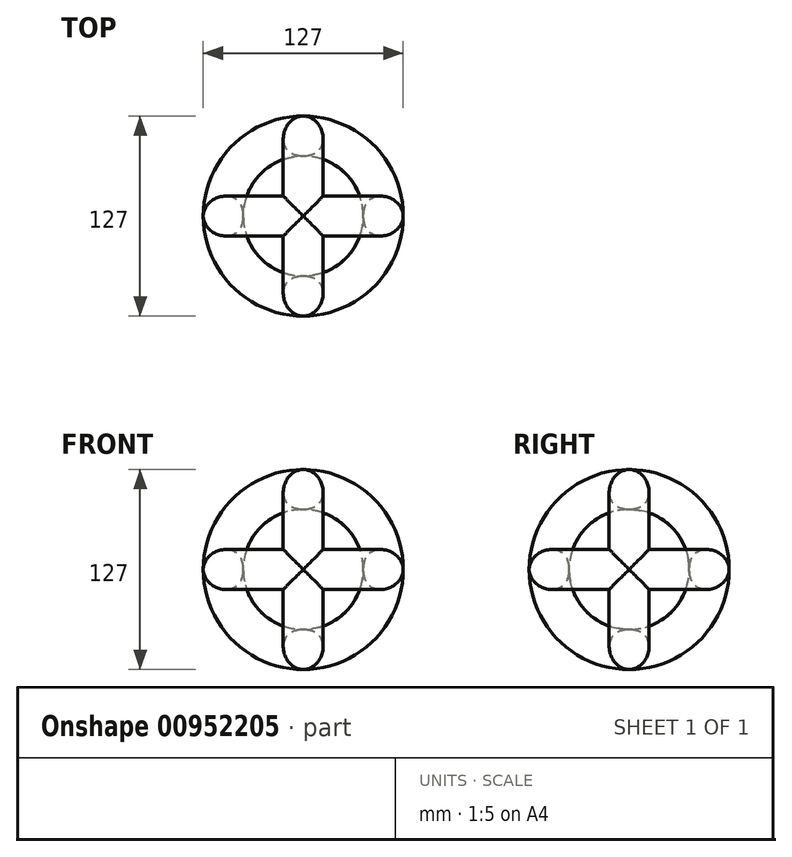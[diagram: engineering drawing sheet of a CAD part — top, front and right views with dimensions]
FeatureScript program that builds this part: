
annotation { "Feature Type Name" : "Feature", "Feature Type Description" : "" }
export const myFeature = defineFeature(function(context is Context, id is Id, definition is map)
    precondition{}
    {
        {
            var Q0;
            Q0=qCreatedBy(makeId("Front.planeOp"),FACE);
            var sketch = newSketch(context, id + "F0", { "sketchPlane" : qUnion([Q0])});
            skCircle(sketch, "E0", {"center": v(50.8, 0) * mm, "radius": 12.7 * mm});
            skCircle(sketch, "E1.1.0", {"center": v(0, 50.8) * mm, "radius": 12.7 * mm});
            skPoint(sketch, "E1.center", {"position": v(0, 0) * mm});
            skSolve(sketch);
        }
        {
            var Q0;
            Q0=qCreatedBy(makeId("Right.planeOp"),FACE);
            var sketch = newSketch(context, id + "F1", { "sketchPlane" : qUnion([Q0])});
            skCircle(sketch, "E2", {"center": v(0, 0) * mm, "radius": 50.8 * mm});
            skSolve(sketch);
        }
        {
            var Q0;
            Q0=qCreatedBy(makeId("Top.planeOp"),FACE);
            var sketch = newSketch(context, id + "F2", { "sketchPlane" : qUnion([Q0])});
            skCircle(sketch, "E3", {"center": v(0, 0) * mm, "radius": 50.8 * mm});
            skSolve(sketch);
        }
        {
            var Q0;
            Q0=makeQuery(id+"F0.imprint","IMPRINT",FACE,{"disambiguationData":[TD([[makeQuery(id+"F0.imprint","IMPRINT",EDGE,{"derivedFrom":sQuery(id+"F0.wireOp",EDGE,"E1.1.0")}),1.0]])]});
            var Q1;
            Q1=sQuery(id+"F1.wireOp",EDGE,"E2");
            sweep(context, id + "F3", {"profiles" : qUnion([Q0]), "path" : qUnion([Q1])});
        }
        {
            var Q0;
            Q0=makeQuery(id+"F0.imprint","IMPRINT",FACE,{"disambiguationData":[TD([[makeQuery(id+"F0.imprint","IMPRINT",EDGE,{"derivedFrom":sQuery(id+"F0.wireOp",EDGE,"E0")}),1.0]])]});
            var Q1;
            Q1=sQuery(id+"F2.wireOp",EDGE,"E3");
            sweep(context, id + "F4", {"operationType" : NewBodyOperationType.ADD, "profiles" : qUnion([Q0]), "path" : qUnion([Q1])});
        }
        {
            var Q0;
            Q0=qCreatedBy(makeId("Right.planeOp"),FACE);
            var sketch = newSketch(context, id + "F5", { "sketchPlane" : qUnion([Q0])});
            skCircle(sketch, "E4", {"center": v(0, -50.8) * mm, "radius": 12.7 * mm});
            skSolve(sketch);
        }
        {
            var Q0;
            Q0=qCreatedBy(makeId("Front.planeOp"),FACE);
            var sketch = newSketch(context, id + "F6", { "sketchPlane" : qUnion([Q0])});
            skCircle(sketch, "E5", {"center": v(0, 0) * mm, "radius": 50.8 * mm});
            skSolve(sketch);
        }
        {
            var Q0;
            Q0 = qSketchRegion(id + "F5", true);
            var Q1;
            Q1 = qConstructionFilter(qBodyType(qCreatedBy(id + "F6" ,EDGE), BodyType.WIRE), ConstructionObject.NO);
            sweep(context, id + "F7", {"operationType" : NewBodyOperationType.ADD, "profiles" : qUnion([Q0]), "path" : qUnion([Q1])});
        }
        {
            var Q0;
            Q0=qCreatedBy(makeId("Top.planeOp"),FACE);
            var sketch = newSketch(context, id + "F8", { "sketchPlane" : qUnion([Q0])});
            skArc(sketch, "E6", {"start": v(0, -38.1) * mm, "mid": v(38.1, 0) * mm, "end": v(0, 38.1) * mm});
            skLineSegment(sketch, "E7", {"start": v(0, 38.1) * mm, "end": v(0, -38.1) * mm});
            skSolve(sketch);
        }
        {
            var Q0;
            Q0=makeQuery(id+"F8.imprint","IMPRINT",FACE,{"disambiguationData":[TD([[makeQuery(id+"F8.imprint","IMPRINT",EDGE,{"derivedFrom":sQuery(id+"F8.wireOp",EDGE,"E6")}),1.0]])]});
            var Q1;
            Q1=sQuery(id+"F8.wireOp",EDGE,"E7");
            revolve(context, id + "F9", {"operationType" : NewBodyOperationType.ADD, "surfaceOperationType" : NewSurfaceOperationType.NEW, "entities" : qUnion([Q0]), "axis" : qUnion([Q1]), "revolveType" : RevolveType.FULL});
        }
    });
